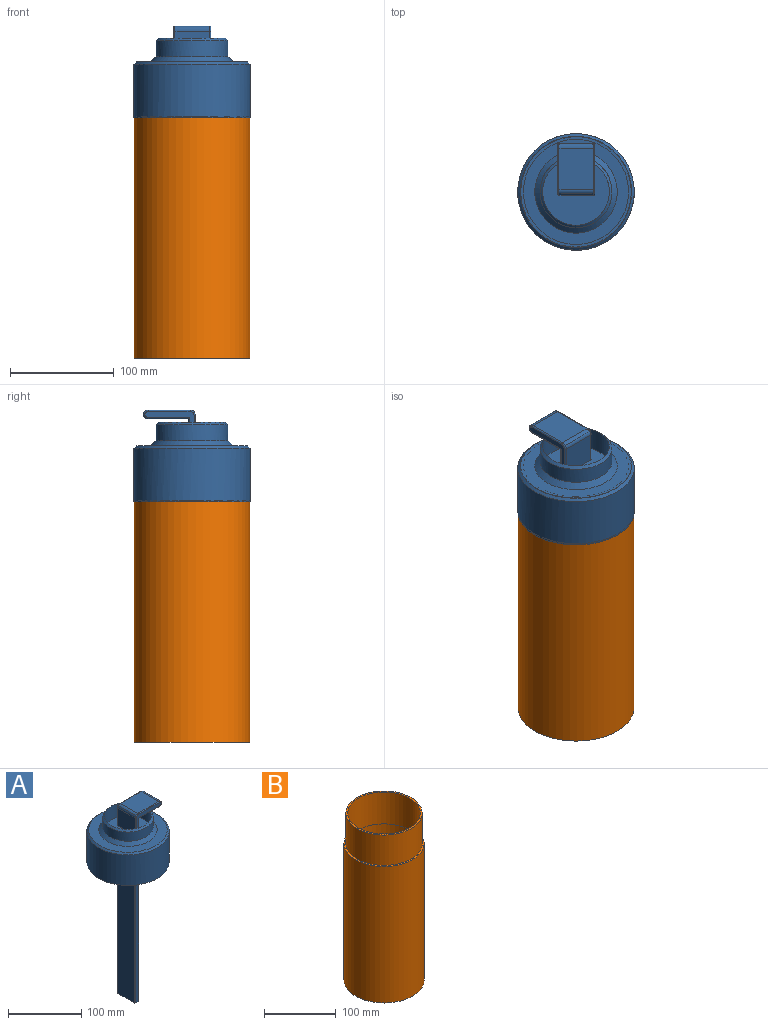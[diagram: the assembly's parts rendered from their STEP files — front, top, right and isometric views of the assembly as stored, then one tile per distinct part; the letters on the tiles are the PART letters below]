
ASSEMBLY  parts=2 mates=1
PART A: 55 faces, bbox 112.1x112.1x314 mm
  f0: plane 4.81x1.16mm, normal (1,0,0), area 5.6mm2, adj f16,f27,f28,f30
  f1: plane 64.11x64.11mm, normal (0,0,1), area 2987.6mm2, adj f17,f21,f22,f23,f24,f37,f43,f44
  f2: plane 106.98x106.98mm, normal (0,0,-1), area 8723.6mm2, adj f5,f6,f7,f8,f9,f51,f52,f53
  f3: cylinder r=56.03mm len=112.06mm, axis (0,0,-1), area 17991.7mm2, adj f11,f20
  f4: plane 106.98x106.98mm, normal (0,0,1), area 4043mm2, adj f18,f20
  f5: cylinder r=53.49mm len=106.98mm, axis (0,0,-1), area 16322.4mm2, adj f2,f11
  f6: plane 276.61x31.63mm, normal (-1,0,0), area 8749.1mm2, adj f2,f10,f51,f54
  f7: plane 276.61x5.24mm, normal (0,1,0), area 1450.2mm2, adj f2,f10,f51,f52
  f8: plane 276.61x31.63mm, normal (1,0,0), area 8749.1mm2, adj f2,f10,f52,f53
  f9: plane 276.61x5.24mm, normal (0,-1,0), area 1450.2mm2, adj f2,f10,f53,f54
  f10: plane 34.17x7.78mm, normal (0,0,-1), area 185.9mm2, adj f6,f7,f8,f9,f13,f14,f15,f16
  f11: cone r=58.57mm half-angle=45deg, axis (0,0,-1), area 1235.9mm2, adj f3,f5
  f12: cylinder r=34.59mm len=69.19mm, axis (0,0,-1), area 3312.6mm2, adj f18,f19
  f13: plane 311.54x29.09mm, normal (1,0,0), area 9062.9mm2, adj f10,f14,f16,f33
  f14: plane 311.54x2.7mm, normal (0,-1,0), area 830.5mm2, adj f10,f13,f15,f28,f30,f31,f32,f33
  f15: plane 306.69x29.09mm, normal (-1,0,0), area 8921.6mm2, adj f10,f14,f16,f28
  f16: plane 311.54x2.7mm, normal (0,1,0), area 830.5mm2, adj f0,f10,f13,f15,f28,f30,f32,f33
  f17: cylinder r=32.05mm len=64.11mm, axis (0,0,-1), area 4604.1mm2, adj f1,f19
  f18: cone r=34.59mm half-angle=45deg, axis (0,0,-1), area 1676.2mm2, adj f4,f12
  f19: cone r=29.51mm half-angle=45deg, axis (0,0,-1), area 752.1mm2, adj f12,f17
  f20: cone r=53.49mm half-angle=45deg, axis (0,0,-1), area 1235.9mm2, adj f3,f4
  f21: plane 33.23x29.4mm, normal (-1,0,0), area 976.8mm2, adj f1,f34,f43,f50
  f22: plane 47.66x33.21mm, normal (0,-1,0), area 394.6mm2, adj f1,f37,f38,f39,f40,f41,f42,f43
  f23: plane 33.23x25.88mm, normal (1,0,0), area 859.8mm2, adj f1,f26,f37,f44
  f24: plane 47.66x33.21mm, normal (0,1,0), area 394.6mm2, adj f1,f44,f45,f46,f47,f48,f49,f50
  f25: plane 40.12x33.23mm, normal (0,0,1), area 1333mm2, adj f34,f35,f41,f48
  f26: plane 38.44x33.23mm, normal (0,0,-1), area 1277.2mm2, adj f23,f36,f38,f45
  f27: plane 48.02x4.81mm, normal (0,1,0), area 228.9mm2, adj f0,f28,f30,f35,f36
  f28: plane 46.76x31.85mm, normal (0,0,1), area 1419.5mm2, adj f0,f14,f15,f16,f27,f29,f31,f36
  f29: plane 48.02x4.81mm, normal (0,-1,0), area 228.9mm2, adj f28,f30,f31,f35,f36
  f30: plane 47.13x31.85mm, normal (0,0,-1), area 1431.3mm2, adj f0,f14,f16,f27,f29,f31,f32,f35
  f31: plane 4.81x1.6mm, normal (1,0,0), area 7.7mm2, adj f14,f28,f29,f30
  f32: plane 29.09x0.05mm, normal (-1,0,0), area 1.4mm2, adj f14,f16,f30,f33
  f33: plane 29.09x2.7mm, normal (0,0,-1), area 78.6mm2, adj f13,f14,f16,f32
  f34: cylinder r=5.08mm len=33.23mm, axis (0,1,0), area 265.2mm2, adj f21,f25,f42,f49
  f35: cylinder r=5.08mm len=33.23mm, axis (0,-1,0), area 163.7mm2, adj f25,f27,f29,f30,f36,f40,f47
  f36: cylinder r=5.08mm len=33.23mm, axis (0,-1,0), area 144.9mm2, adj f26,f27,f28,f29,f35,f39,f46
  f37: cylinder r=1.27mm len=27.15mm, axis (0,0,1), area 52.5mm2, adj f1,f22,f23,f38
  f38: cylinder r=1.27mm len=39.71mm, axis (-1,0,0), area 77.6mm2, adj f22,f26,f37,f39
  f39: torus R=3.81mm, axis (0,1,0), area 12.9mm2, adj f22,f36,f38,f40
  f40: torus R=3.81mm, axis (0,1,0), area 12.9mm2, adj f22,f35,f39,f41
  f41: cylinder r=1.27mm len=40.12mm, axis (-1,0,0), area 80mm2, adj f22,f25,f40,f42
  f42: torus R=3.81mm, axis (0,1,0), area 14.5mm2, adj f22,f34,f41,f43
  f43: cylinder r=1.27mm len=29.4mm, axis (0,0,-1), area 58.6mm2, adj f1,f21,f22,f42
  f44: cylinder r=1.27mm len=27.15mm, axis (0,0,-1), area 52.5mm2, adj f1,f23,f24,f45
  f45: cylinder r=1.27mm len=39.71mm, axis (1,0,0), area 77.6mm2, adj f24,f26,f44,f46
  f46: torus R=3.81mm, axis (0,1,0), area 12.9mm2, adj f24,f36,f45,f47
  f47: torus R=3.81mm, axis (0,1,0), area 12.9mm2, adj f24,f35,f46,f48
  f48: cylinder r=1.27mm len=40.12mm, axis (1,0,0), area 80mm2, adj f24,f25,f47,f49
  f49: torus R=3.81mm, axis (0,1,0), area 14.5mm2, adj f24,f34,f48,f50
  f50: cylinder r=1.27mm len=29.4mm, axis (0,0,1), area 58.6mm2, adj f1,f21,f24,f49
  f51: cylinder r=1.27mm len=276.61mm, axis (0,0,1), area 551.8mm2, adj f2,f6,f7,f10
  f52: cylinder r=1.27mm len=276.61mm, axis (0,0,-1), area 551.8mm2, adj f2,f7,f8,f10
  f53: cylinder r=1.27mm len=276.61mm, axis (0,0,1), area 551.8mm2, adj f2,f8,f9,f10
  f54: cylinder r=1.27mm len=276.61mm, axis (0,0,-1), area 551.8mm2, adj f2,f6,f9,f10
PART B: 11 faces, bbox 111.5x111.5x284.1 mm
  f0: cylinder r=53.1mm len=106.2mm, axis (0,0,-1), area 17254.6mm2, adj f1,f6
  f1: plane 106.2x106.2mm, normal (0,0,1), area 827.2mm2, adj f0,f2
  f2: cylinder r=50.56mm len=101.12mm, axis (0,0,-1), area 17236.1mm2, adj f1,f9
  f3: cylinder r=53.1mm len=106.2mm, axis (0,0,1), area 1399.9mm2, adj f5,f7
  f4: cylinder r=55.73mm len=232.41mm, axis (0,0,1), area 81374.8mm2, adj f5,f6
  f5: plane 111.45x111.45mm, normal (0,0,-1), area 897.9mm2, adj f3,f4
  f6: plane 111.45x111.45mm, normal (0,0,1), area 897.9mm2, adj f0,f4
  f7: plane 106.2x106.2mm, normal (0,0,-1), area 8857.8mm2, adj f3
  f8: cylinder r=53.19mm len=223.13mm, axis (0,0,1), area 74566mm2, adj f9,f10
  f9: plane 106.37x106.37mm, normal (0,0,-1), area 856mm2, adj f2,f8
  f10: plane 106.37x106.37mm, normal (0,0,1), area 8886.6mm2, adj f8
PLACE A rot(axis=(0,0,1),90deg) t=(-39.85,-114.78,-51.13)mm
PLACE B t=(-39.85,-114.78,-47.32)mm fixed
MATE fastened B.f0 <-> A.f3  axis (0,0,1) through (-39.85,-114.78,-47.32)mm
